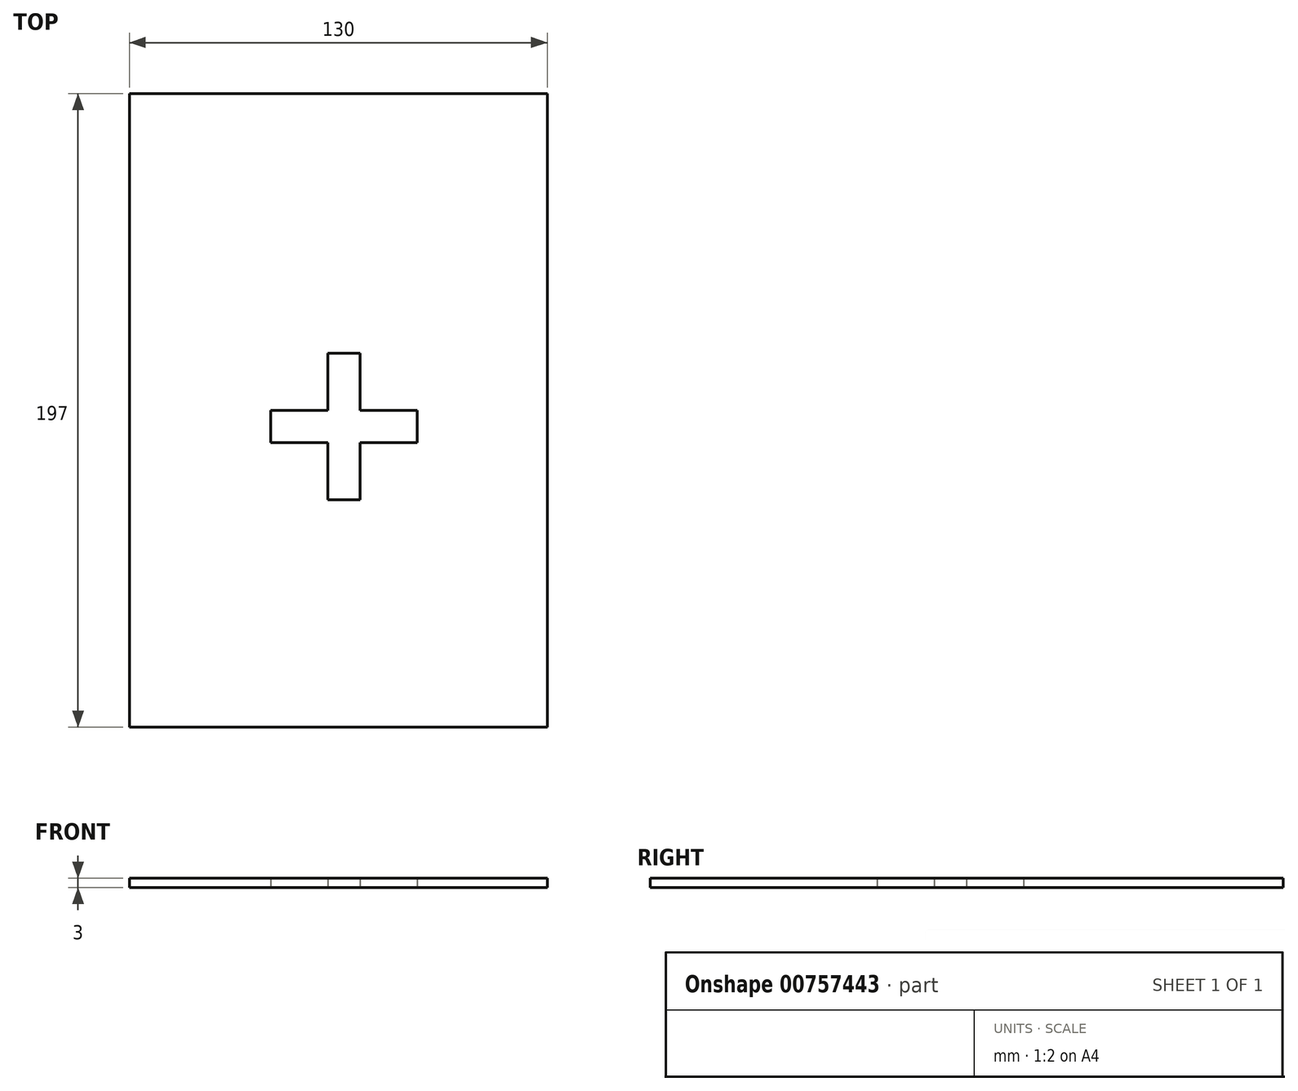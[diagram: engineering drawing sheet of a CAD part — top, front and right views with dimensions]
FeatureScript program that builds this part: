
annotation { "Feature Type Name" : "Feature", "Feature Type Description" : "" }
export const myFeature = defineFeature(function(context is Context, id is Id, definition is map)
    precondition{}
    {
        {
            var Q0;
            Q0=qCreatedBy(makeId("Top.planeOp"),FACE);
            var sketch = newSketch(context, id + "F0", { "sketchPlane" : qUnion([Q0])});
            skLineSegment(sketch, "E0.bottom", {"start": v(-65, 98.5) * mm, "end": v(65, 98.5) * mm});
            skLineSegment(sketch, "E0.top", {"start": v(-65, -98.5) * mm, "end": v(65, -98.5) * mm});
            skLineSegment(sketch, "E0.left", {"start": v(-65, 98.5) * mm, "end": v(-65, -98.5) * mm});
            skLineSegment(sketch, "E0.right", {"start": v(65, 98.5) * mm, "end": v(65, -98.5) * mm});
            skPoint(sketch, "E0.middle", {"position": v(0, 0) * mm});
            skSolve(sketch);
        }
        {
            var Q0;
            Q0=makeQuery(id+"F0.imprint","IMPRINT",FACE,{"disambiguationData":[TD([[makeQuery(id+"F0.imprint","IMPRINT",EDGE,{"derivedFrom":sQuery(id+"F0.wireOp",EDGE,"E0.bottom")}),-1.0]])]});
            extrude(context, id + "F1", {"entities" : qUnion([Q0]), "depth" : 3 * mm, "offsetDistance" : 25.4 * mm});
        }
        {
            var Q0;
            Q0=qCreatedBy(makeId("Top.planeOp"),FACE);
            var sketch = newSketch(context, id + "F2", { "sketchPlane" : qUnion([Q0])});
            skLineSegment(sketch, "E1", {"start": v(6.76, 17.78) * mm, "end": v(-3.24, 17.78) * mm});
            skLineSegment(sketch, "E2", {"start": v(-3.24, 17.78) * mm, "end": v(-3.24, 0) * mm});
            skLineSegment(sketch, "E3", {"start": v(-3.24, 0) * mm, "end": v(-21.02, 0) * mm});
            skLineSegment(sketch, "E4", {"start": v(-21.02, 0) * mm, "end": v(-21.02, -10) * mm});
            skLineSegment(sketch, "E5", {"start": v(-21.02, -10) * mm, "end": v(-3.24, -10) * mm});
            skLineSegment(sketch, "E6", {"start": v(-3.24, -10) * mm, "end": v(-3.24, -27.79) * mm});
            skLineSegment(sketch, "E7", {"start": v(-3.24, -27.79) * mm, "end": v(6.77, -27.79) * mm});
            skLineSegment(sketch, "E8", {"start": v(6.77, -27.79) * mm, "end": v(6.77, -10) * mm});
            skLineSegment(sketch, "E9", {"start": v(24.55, -10) * mm, "end": v(6.77, -10) * mm});
            skLineSegment(sketch, "E10", {"start": v(24.55, -10) * mm, "end": v(24.55, 0) * mm});
            skLineSegment(sketch, "E11", {"start": v(24.55, 0) * mm, "end": v(6.76, 0) * mm});
            skLineSegment(sketch, "E12", {"start": v(6.76, 0) * mm, "end": v(6.76, 17.78) * mm});
            skSolve(sketch);
        }
        {
            var Q0;
            Q0 = qSketchRegion(id + "F2", true);
            extrude(context, id + "F3", {"entities" : qUnion([Q0]), "operationType" : NewBodyOperationType.REMOVE, "depth" : 9.65 * mm, "offsetDistance" : 25.4 * mm});
        }
    });
